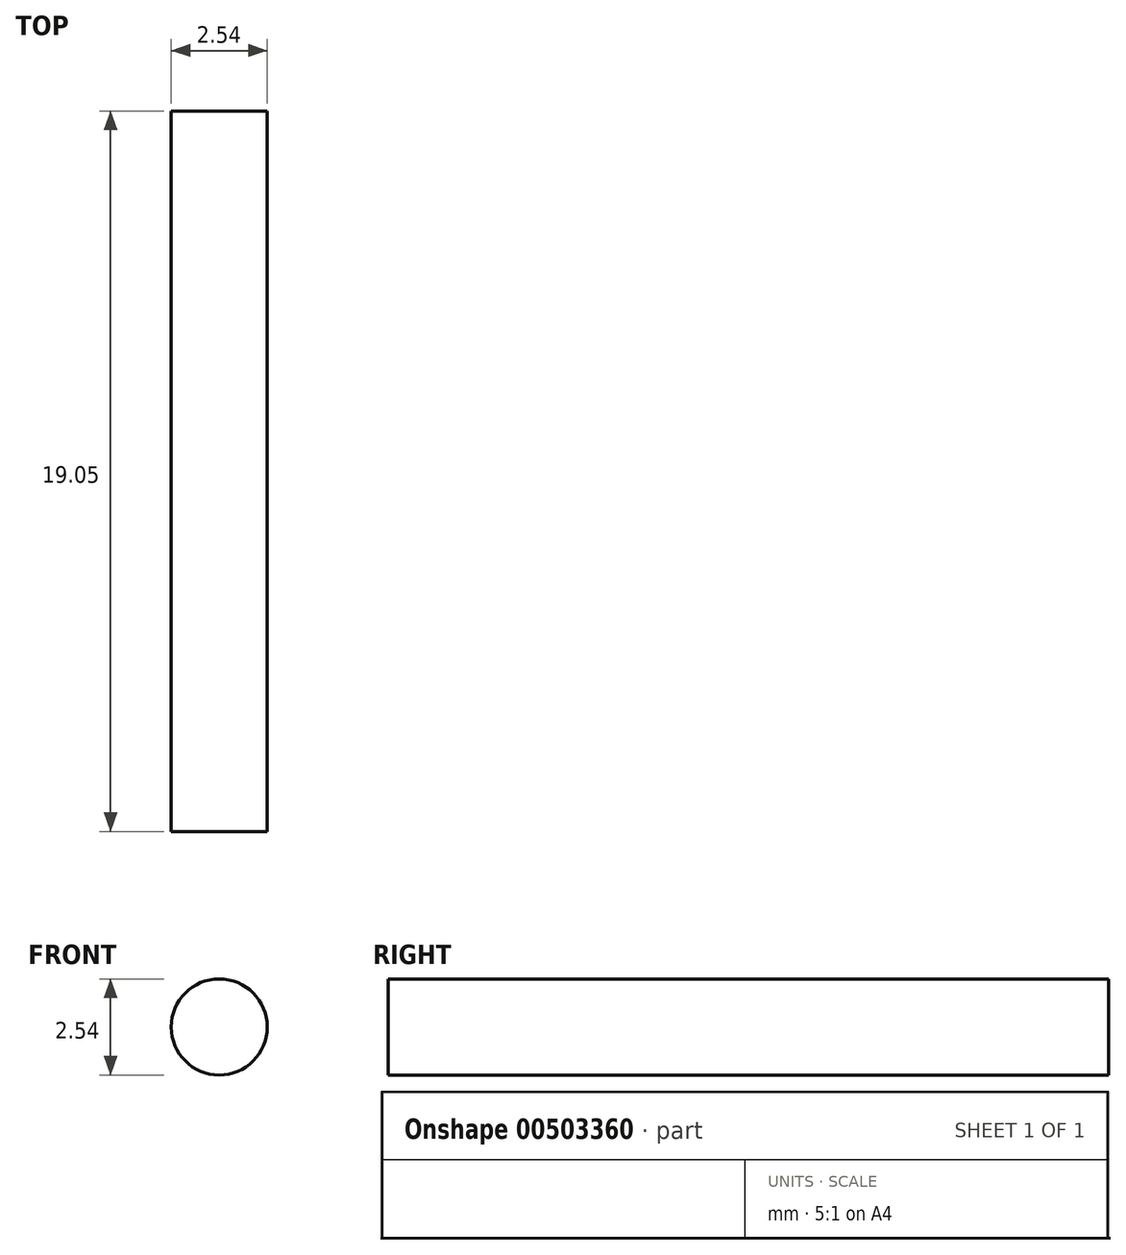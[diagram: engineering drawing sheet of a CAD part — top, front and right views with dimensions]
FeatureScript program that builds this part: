
annotation { "Feature Type Name" : "Feature", "Feature Type Description" : "" }
export const myFeature = defineFeature(function(context is Context, id is Id, definition is map)
    precondition{}
    {
        {
            var Q0;
            Q0=qCreatedBy(makeId("Front.planeOp"),FACE);
            var sketch = newSketch(context, id + "F0", { "sketchPlane" : qUnion([Q0])});
            skCircle(sketch, "E0", {"center": v(0, 0) * mm, "radius": 1.27 * mm});
            skSolve(sketch);
        }
        {
            var Q0;
            Q0=makeQuery(id+"F0.imprint","IMPRINT",FACE,{"disambiguationData":[TD([[makeQuery(id+"F0.imprint","IMPRINT",EDGE,{"derivedFrom":sQuery(id+"F0.wireOp",EDGE,"E0")}),1.0]])]});
            extrude(context, id + "F1", {"entities" : qUnion([Q0]), "depth" : 19.05 * mm});
        }
    });
